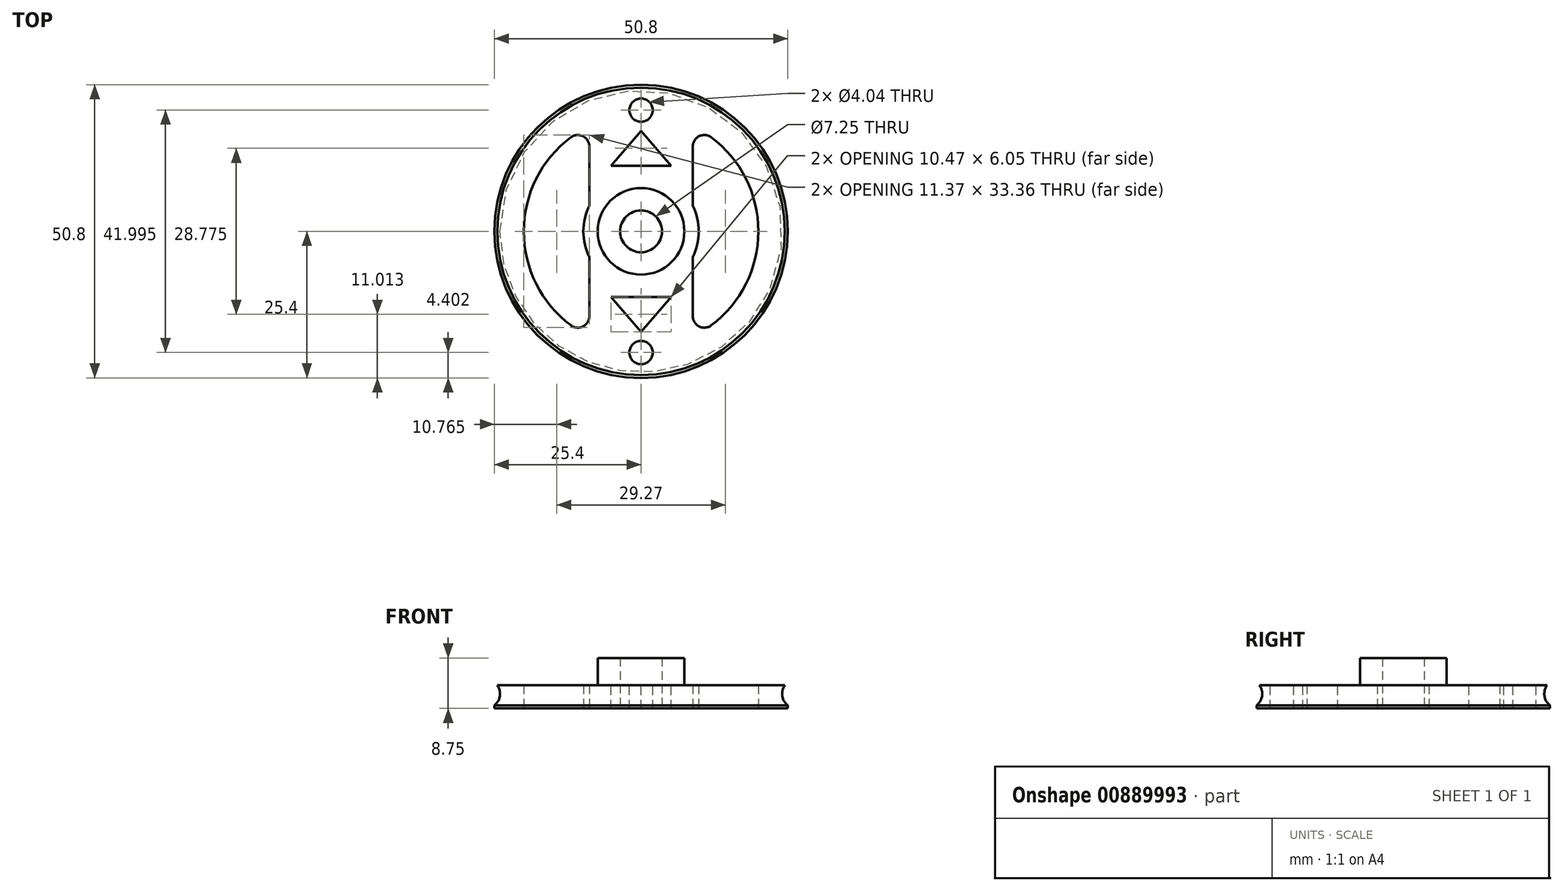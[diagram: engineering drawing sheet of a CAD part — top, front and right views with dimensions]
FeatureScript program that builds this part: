
annotation { "Feature Type Name" : "Feature", "Feature Type Description" : "" }
export const myFeature = defineFeature(function(context is Context, id is Id, definition is map)
    precondition{}
    {
        {
            var Q0;
            Q0=qCreatedBy(makeId("Top.planeOp"),FACE);
            var sketch = newSketch(context, id + "F0", { "sketchPlane" : qUnion([Q0])});
            skCircle(sketch, "E0", {"center": v(0, 0) * mm, "radius": 25.4 * mm});
            skCircle(sketch, "E1", {"center": v(0, 0) * mm, "radius": 3.63 * mm});
            skArc(sketch, "E2", {"start": v(-8.95, 4.46) * mm, "mid": v(-10, 0) * mm, "end": v(-8.95, -4.46) * mm});
            skArc(sketch, "E3.0", {"start": v(-12.15, 16.3) * mm, "mid": v(-20.32, 0) * mm, "end": v(-12.15, -16.3) * mm});
            skLineSegment(sketch, "E4.0", {"start": v(-8.95, 14.69) * mm, "end": v(-8.95, 4.46) * mm});
            skLineSegment(sketch, "E5.0", {"start": v(8.95, 14.69) * mm, "end": v(8.95, 4.46) * mm});
            skPoint(sketch, "E6.orphan", {"position": v(0, 22.46) * mm});
            skPoint(sketch, "E7.visualSharp", {"position": v(-8.95, 18.24) * mm});
            skArc(sketch, "E7.filletArc", {"start": v(-8.95, 14.69) * mm, "mid": v(-10.05, 16.47) * mm, "end": v(-12.15, 16.3) * mm});
            skPoint(sketch, "E8.visualSharp", {"position": v(8.95, 18.24) * mm});
            skArc(sketch, "E8.filletArc", {"start": v(12.15, 16.3) * mm, "mid": v(10.05, 16.47) * mm, "end": v(8.95, 14.69) * mm});
            skArc(sketch, "E9.1.0", {"start": v(-12.15, -16.3) * mm, "mid": v(-10.05, -16.47) * mm, "end": v(-8.95, -14.69) * mm});
            skArc(sketch, "E9.1.1", {"start": v(8.95, -14.69) * mm, "mid": v(10.05, -16.47) * mm, "end": v(12.15, -16.3) * mm});
            skLineSegment(sketch, "E9.1.2", {"start": v(8.95, -14.69) * mm, "end": v(8.95, -4.46) * mm});
            skLineSegment(sketch, "E9.1.3", {"start": v(-8.95, -14.69) * mm, "end": v(-8.95, -4.46) * mm});
            skArc(sketch, "E10.trimOffspring", {"start": v(12.15, -16.3) * mm, "mid": v(20.32, 0) * mm, "end": v(12.15, 16.3) * mm});
            skArc(sketch, "E11.trimOffspring", {"start": v(8.95, -4.46) * mm, "mid": v(10, 0) * mm, "end": v(8.95, 4.46) * mm});
            skSolve(sketch);
        }
        {
            var Q0;
            Q0=makeQuery(id+"F0.imprint","IMPRINT",FACE,{"disambiguationData":[TD([[makeQuery(id+"F0.imprint","IMPRINT",EDGE,{"derivedFrom":sQuery(id+"F0.wireOp",EDGE,"E0")}),1.0]])]});
            extrude(context, id + "F1", {"entities" : qUnion([Q0]), "depth" : 4 * mm, "offsetDistance" : 25.4 * mm});
        }
        {
            var Q0;
            Q0=makeQuery(id+"F1.opExtrude","CAP_FACE",FACE,{"disambiguationData":[OSD([sQuery(id+"F0.wireOp",EDGE,"E0"),sQuery(id+"F0.wireOp",EDGE,"E1"),sQuery(id+"F0.wireOp",EDGE,"E2"),sQuery(id+"F0.wireOp",EDGE,"E3.0"),sQuery(id+"F0.wireOp",EDGE,"E4.0"),sQuery(id+"F0.wireOp",EDGE,"E5.0"),sQuery(id+"F0.wireOp",EDGE,"E7.filletArc"),sQuery(id+"F0.wireOp",EDGE,"E8.filletArc"),sQuery(id+"F0.wireOp",EDGE,"E9.1.0"),sQuery(id+"F0.wireOp",EDGE,"E9.1.1"),sQuery(id+"F0.wireOp",EDGE,"E9.1.2"),sQuery(id+"F0.wireOp",EDGE,"E9.1.3"),sQuery(id+"F0.wireOp",EDGE,"E10.trimOffspring"),sQuery(id+"F0.wireOp",EDGE,"E11.trimOffspring")])],"isStart":false});
            var sketch = newSketch(context, id + "F2", { "sketchPlane" : qUnion([Q0])});
            skCircle(sketch, "E12", {"center": v(0, 0) * mm, "radius": 7.5 * mm});
            skSolve(sketch);
        }
        {
            var Q0;
            Q0=makeQuery(id+"F2.imprint","IMPRINT",FACE,{"disambiguationData":[TD([[makeQuery(id+"F2.imprint","IMPRINT",EDGE,{"derivedFrom":sQuery(id+"F2.wireOp",EDGE,"E12")}),1.0]])]});
            extrude(context, id + "F3", {"entities" : qUnion([Q0]), "operationType" : NewBodyOperationType.ADD, "depth" : 4.75 * mm, "offsetDistance" : 25.4 * mm});
        }
        {
            var Q0;
            Q0=makeQuery(id+"F1.opExtrude","CAP_FACE",FACE,{"disambiguationData":[OSD([sQuery(id+"F0.wireOp",EDGE,"E0"),sQuery(id+"F0.wireOp",EDGE,"E1"),sQuery(id+"F0.wireOp",EDGE,"E2"),sQuery(id+"F0.wireOp",EDGE,"E3.0"),sQuery(id+"F0.wireOp",EDGE,"E4.0"),sQuery(id+"F0.wireOp",EDGE,"E5.0"),sQuery(id+"F0.wireOp",EDGE,"E7.filletArc"),sQuery(id+"F0.wireOp",EDGE,"E8.filletArc"),sQuery(id+"F0.wireOp",EDGE,"E9.1.0"),sQuery(id+"F0.wireOp",EDGE,"E9.1.1"),sQuery(id+"F0.wireOp",EDGE,"E9.1.2"),sQuery(id+"F0.wireOp",EDGE,"E9.1.3"),sQuery(id+"F0.wireOp",EDGE,"E10.trimOffspring"),sQuery(id+"F0.wireOp",EDGE,"E11.trimOffspring")])],"isStart":false});
            var sketch = newSketch(context, id + "F4", { "sketchPlane" : qUnion([Q0])});
            skLineSegment(sketch, "E13", {"start": v(0, 11.36) * mm, "end": v(-5.23, 11.36) * mm});
            skLineSegment(sketch, "E14", {"start": v(-5.23, 11.36) * mm, "end": v(0, 17.41) * mm});
            skLineSegment(sketch, "E15", {"start": v(0, 17.41) * mm, "end": v(0, 11.36) * mm});
            skLineSegment(sketch, "E16.MirrorCS", {"start": v(0, 11.36) * mm, "end": v(5.23, 11.36) * mm});
            skLineSegment(sketch, "E17.MirrorCS", {"start": v(5.23, 11.36) * mm, "end": v(0, 17.41) * mm});
            skLineSegment(sketch, "E18.1.0", {"start": v(-5.23, -11.36) * mm, "end": v(0, -17.41) * mm});
            skLineSegment(sketch, "E18.1.1", {"start": v(5.23, -11.36) * mm, "end": v(0, -17.41) * mm});
            skLineSegment(sketch, "E18.1.2", {"start": v(0, -11.36) * mm, "end": v(-5.23, -11.36) * mm});
            skLineSegment(sketch, "E18.1.3", {"start": v(0, -11.36) * mm, "end": v(5.23, -11.36) * mm});
            skPoint(sketch, "E18.center", {"position": v(0, 0) * mm});
            skCircle(sketch, "E19", {"center": v(0, 21) * mm, "radius": 2.02 * mm});
            skCircle(sketch, "E20.1.0", {"center": v(0, -21) * mm, "radius": 2.02 * mm});
            skSolve(sketch);
        }
        {
            var Q0;
            Q0=qSketchRegion(id+"F4",true);
            extrude(context, id + "F5", {"entities" : qUnion([Q0]), "operationType" : NewBodyOperationType.REMOVE, "endBound" : BoundingType.THROUGH_ALL, "oppositeDirection" : true, "depth" : 25.4 * mm, "offsetDistance" : 25.4 * mm});
        }
        {
            var Q0;
            Q0=qCreatedBy(makeId("Front.planeOp"),FACE);
            var sketch = newSketch(context, id + "F6", { "sketchPlane" : qUnion([Q0])});
            skCircle(sketch, "E21", {"center": v(-26.92, 2.53) * mm, "radius": 2.5 * mm});
            skLineSegment(sketch, "E22", {"start": v(0, 14.96) * mm, "end": v(0, -0.92) * mm, "construction": true});
            skSolve(sketch);
        }
        {
            var Q0;
            Q0 = qSketchRegion(id + "F6", true);
            var Q1;
            Q1=sQuery(id+"F6.wireOp",EDGE,"E22");
            revolve(context, id + "F7", {"operationType" : NewBodyOperationType.REMOVE, "surfaceOperationType" : NewSurfaceOperationType.NEW, "entities" : qUnion([Q0]), "axis" : qUnion([Q1]), "revolveType" : RevolveType.FULL, "oppositeDirection" : true});
        }
    });
